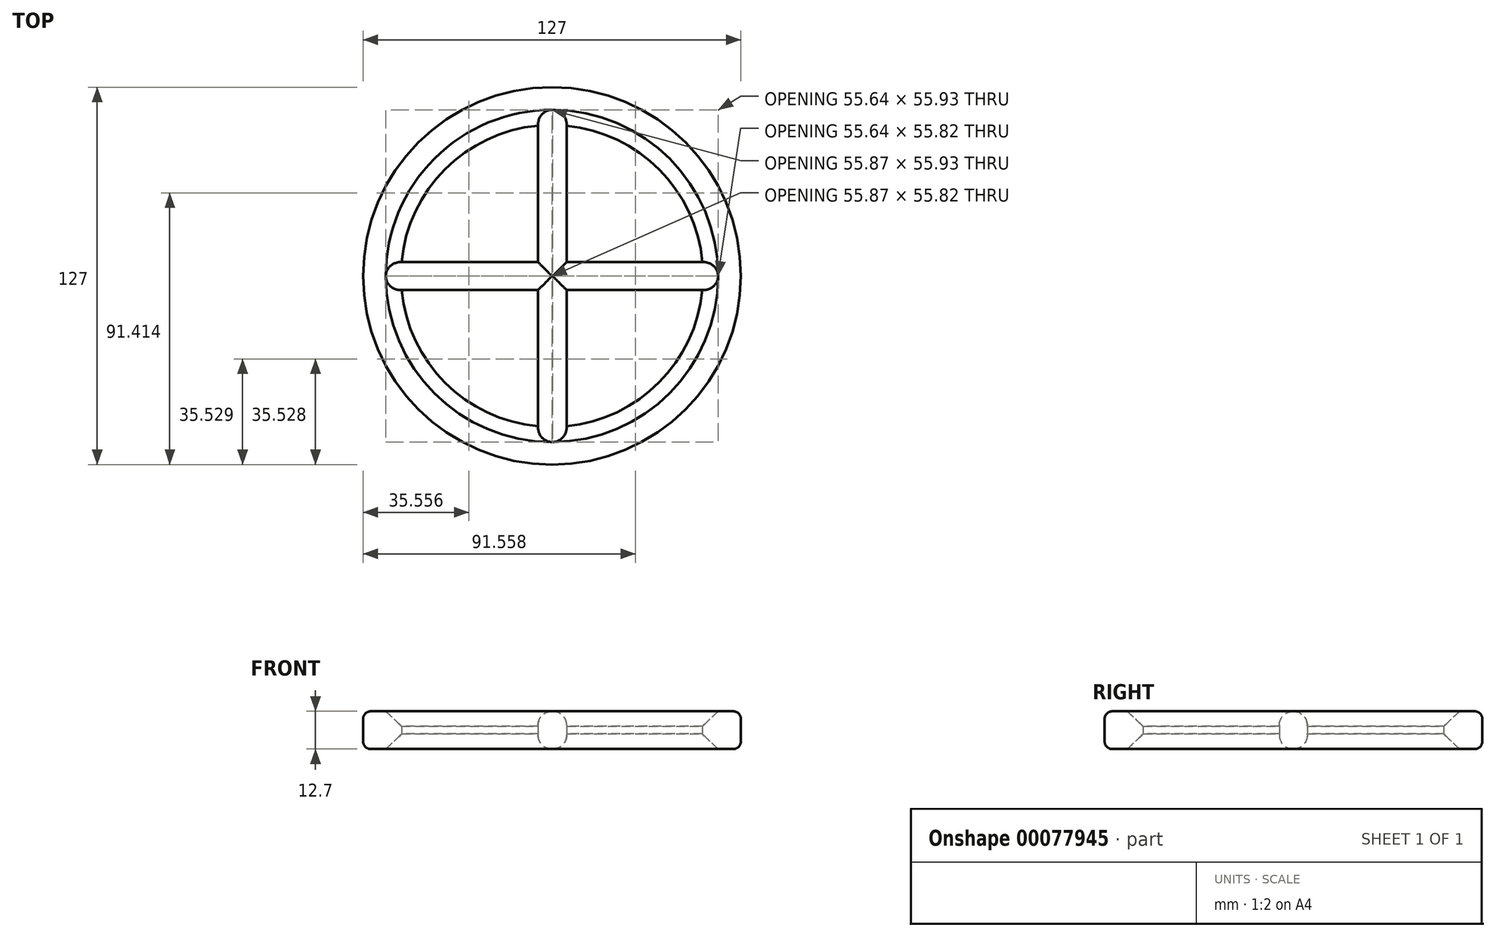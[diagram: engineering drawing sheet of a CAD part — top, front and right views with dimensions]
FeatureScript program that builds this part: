
annotation { "Feature Type Name" : "Feature", "Feature Type Description" : "" }
export const myFeature = defineFeature(function(context is Context, id is Id, definition is map)
    precondition{}
    {
        {
            var Q0;
            Q0=qCreatedBy(makeId("Top.planeOp"),FACE);
            var sketch = newSketch(context, id + "F0", { "sketchPlane" : qUnion([Q0])});
            skCircle(sketch, "E0", {"center": v(0, 0) * mm, "radius": 63.5 * mm});
            skArc(sketch, "E1", {"start": v(50.59, 4.65) * mm, "mid": v(36.02, 35.82) * mm, "end": v(4.94, 50.56) * mm});
            skLineSegment(sketch, "E2.bottom", {"start": v(-50.59, 4.65) * mm, "end": v(-4.71, 4.65) * mm});
            skLineSegment(sketch, "E2.top", {"start": v(-50.58, -4.77) * mm, "end": v(-4.71, -4.77) * mm});
            skLineSegment(sketch, "E3.left", {"start": v(-4.71, 50.58) * mm, "end": v(-4.71, 4.65) * mm});
            skLineSegment(sketch, "E3.right", {"start": v(4.94, 50.56) * mm, "end": v(4.94, 4.65) * mm});
            skLineSegment(sketch, "E4.trimOffspring", {"start": v(4.94, 4.65) * mm, "end": v(50.59, 4.65) * mm});
            skLineSegment(sketch, "E5.trimOffspring", {"start": v(-4.71, -4.77) * mm, "end": v(-4.71, -50.58) * mm});
            skLineSegment(sketch, "E6.trimOffspring", {"start": v(4.94, -4.77) * mm, "end": v(4.94, -50.56) * mm});
            skLineSegment(sketch, "E7.trimOffspring", {"start": v(4.94, -4.77) * mm, "end": v(50.58, -4.77) * mm});
            skArc(sketch, "E8.trimOffspring", {"start": v(4.94, -50.56) * mm, "mid": v(35.98, -35.86) * mm, "end": v(50.58, -4.77) * mm});
            skArc(sketch, "E9.trimOffspring", {"start": v(-50.58, -4.77) * mm, "mid": v(-35.9, -35.94) * mm, "end": v(-4.71, -50.58) * mm});
            skArc(sketch, "E10.trimOffspring", {"start": v(-4.71, 50.58) * mm, "mid": v(-35.94, 35.9) * mm, "end": v(-50.59, 4.65) * mm});
            skSolve(sketch);
        }
        {
            var Q0;
            Q0 = qSketchRegion(id + "F0", true);
            extrude(context, id + "F1", {"entities" : qUnion([Q0]), "depth" : 12.7 * mm});
        }
        {
            var Q0;
            Q0=makeQuery(id+"F1.opExtrude","CAP_EDGE",EDGE,{"disambiguationData":[OSD([sQuery(id+"F0.wireOp",EDGE,"E0")])],"isStart":false});
            var Q1;
            Q1=makeQuery(id+"F1.opExtrude","CAP_EDGE",EDGE,{"disambiguationData":[OSD([sQuery(id+"F0.wireOp",EDGE,"E0")])],"isStart":true});
            fillet(context, id + "F2", {"entities" : qUnion([Q0, Q1]), "radius" : 2.54 * mm, "tangentPropagation" : true, "allowEdgeOverflow" : false});
        }
        {
            var Q0;
            Q0=makeQuery(id+"F1.opExtrude","CAP_EDGE",EDGE,{"disambiguationData":[OSD([sQuery(id+"F0.wireOp",EDGE,"E2.top")])],"isStart":false});
            var Q1;
            Q1=makeQuery(id+"F1.opExtrude","CAP_EDGE",EDGE,{"disambiguationData":[OSD([sQuery(id+"F0.wireOp",EDGE,"E2.bottom")])],"isStart":false});
            var Q2;
            Q2=makeQuery(id+"F1.opExtrude","CAP_EDGE",EDGE,{"disambiguationData":[OSD([sQuery(id+"F0.wireOp",EDGE,"E2.top")])],"isStart":true});
            var Q3;
            Q3=makeQuery(id+"F1.opExtrude","CAP_EDGE",EDGE,{"disambiguationData":[OSD([sQuery(id+"F0.wireOp",EDGE,"E5.trimOffspring")])],"isStart":false});
            var Q4;
            Q4=makeQuery(id+"F1.opExtrude","CAP_EDGE",EDGE,{"disambiguationData":[OSD([sQuery(id+"F0.wireOp",EDGE,"E6.trimOffspring")])],"isStart":false});
            var Q5;
            Q5=makeQuery(id+"F1.opExtrude","CAP_EDGE",EDGE,{"disambiguationData":[OSD([sQuery(id+"F0.wireOp",EDGE,"E7.trimOffspring")])],"isStart":false});
            var Q6;
            Q6=makeQuery(id+"F1.opExtrude","CAP_EDGE",EDGE,{"disambiguationData":[OSD([sQuery(id+"F0.wireOp",EDGE,"E3.right")])],"isStart":true});
            var Q7;
            Q7=makeQuery(id+"F1.opExtrude","CAP_EDGE",EDGE,{"disambiguationData":[OSD([sQuery(id+"F0.wireOp",EDGE,"E3.right")])],"isStart":false});
            var Q8;
            Q8=makeQuery(id+"F1.opExtrude","CAP_EDGE",EDGE,{"disambiguationData":[OSD([sQuery(id+"F0.wireOp",EDGE,"E3.left")])],"isStart":false});
            var Q9;
            Q9=makeQuery(id+"F1.opExtrude","CAP_EDGE",EDGE,{"disambiguationData":[OSD([sQuery(id+"F0.wireOp",EDGE,"E4.trimOffspring")])],"isStart":false});
            var Q10;
            Q10=makeQuery(id+"F1.opExtrude","CAP_EDGE",EDGE,{"disambiguationData":[OSD([sQuery(id+"F0.wireOp",EDGE,"E7.trimOffspring")])],"isStart":true});
            var Q11;
            Q11=makeQuery(id+"F1.opExtrude","CAP_EDGE",EDGE,{"disambiguationData":[OSD([sQuery(id+"F0.wireOp",EDGE,"E6.trimOffspring")])],"isStart":true});
            var Q12;
            Q12=makeQuery(id+"F1.opExtrude","CAP_EDGE",EDGE,{"disambiguationData":[OSD([sQuery(id+"F0.wireOp",EDGE,"E2.bottom")])],"isStart":true});
            var Q13;
            Q13=makeQuery(id+"F1.opExtrude","CAP_EDGE",EDGE,{"disambiguationData":[OSD([sQuery(id+"F0.wireOp",EDGE,"E3.left")])],"isStart":true});
            var Q14;
            Q14=makeQuery(id+"F1.opExtrude","CAP_EDGE",EDGE,{"disambiguationData":[OSD([sQuery(id+"F0.wireOp",EDGE,"E5.trimOffspring")])],"isStart":true});
            var Q15;
            Q15=makeQuery(id+"F1.opExtrude","CAP_EDGE",EDGE,{"disambiguationData":[OSD([sQuery(id+"F0.wireOp",EDGE,"E4.trimOffspring")])],"isStart":true});
            fillet(context, id + "F3", {"entities" : qUnion([Q0, Q1, Q2, Q3, Q4, Q5, Q6, Q7, Q8, Q9, Q10, Q11, Q12, Q13, Q14, Q15]), "radius" : 4.7 * mm, "tangentPropagation" : true, "allowEdgeOverflow" : false});
        }
        {
            var Q0;
            Q0=makeQuery(id+"F1.opExtrude","CAP_EDGE",EDGE,{"disambiguationData":[OSD([sQuery(id+"F0.wireOp",EDGE,"E10.trimOffspring")])],"isStart":false});
            var Q1;
            Q1=makeQuery(id+"F1.opExtrude","CAP_EDGE",EDGE,{"disambiguationData":[OSD([sQuery(id+"F0.wireOp",EDGE,"E9.trimOffspring")])],"isStart":false});
            var Q2;
            Q2=makeQuery(id+"F1.opExtrude","CAP_EDGE",EDGE,{"disambiguationData":[OSD([sQuery(id+"F0.wireOp",EDGE,"E9.trimOffspring")])],"isStart":true});
            var Q3;
            Q3=makeQuery(id+"F1.opExtrude","CAP_EDGE",EDGE,{"disambiguationData":[OSD([sQuery(id+"F0.wireOp",EDGE,"E10.trimOffspring")])],"isStart":true});
            var Q4;
            Q4=makeQuery(id+"F1.opExtrude","CAP_EDGE",EDGE,{"disambiguationData":[OSD([sQuery(id+"F0.wireOp",EDGE,"E1")])],"isStart":true});
            var Q5;
            Q5=makeQuery(id+"F1.opExtrude","CAP_EDGE",EDGE,{"disambiguationData":[OSD([sQuery(id+"F0.wireOp",EDGE,"E8.trimOffspring")])],"isStart":true});
            var Q6;
            Q6=makeQuery(id+"F1.opExtrude","CAP_EDGE",EDGE,{"disambiguationData":[OSD([sQuery(id+"F0.wireOp",EDGE,"E8.trimOffspring")])],"isStart":false});
            var Q7;
            Q7=makeQuery(id+"F1.opExtrude","CAP_EDGE",EDGE,{"disambiguationData":[OSD([sQuery(id+"F0.wireOp",EDGE,"E1")])],"isStart":false});
            chamfer(context, id + "F4", {"entities" : qUnion([Q0, Q1, Q2, Q3, Q4, Q5, Q6, Q7]), "width" : 5.08 * mm, "tangentPropagation" : true});
        }
    });
